# Revit family: NWL_Elevator_Artisan_Rectangular_42x32
name_source: partatom
category: Specialty Equipment
units: mm (PartAtom-declared; Revit-internal decimal feet)

## family parameters
Always vertical = Yes
Cut with Voids When Loaded = No
Enable Cutting in Views = No
Maintain Annotation Orientation = No
Part Type = Normal
Room Calculation Point = No
Round Connector Dimension = Use Diameter
Shared = No
Work Plane-Based = No

## types (1)
- NWL_Elevator_Artisan_Rectangular_42x32
    Cab_Height = 78 "
    Construction Details = https://www.arcat.com
    Default Elevation = 0 "
    Frame = Steel
    Glass = Glass
    Green Building-LEED = https://www.arcat.com
    Hoistway_Length = 39.106 "
    Hoistway_Width = 28.106 "
    Load = 30 VA
    Machine_Height = 18 "
    Manufacturer = Nationwide Lifts
    Manufacturer Fax = (877) 825-6001
    Manufacturer Website = https://www.elevators.com
    Model = Artisan Rectangular 42x32
    Platform_Length = 36.606 "
    Platform_Width = 25.606 "
    Poles = 1
    Product Data = https://www.arcat.com
    Ring_Length = 42 "
    Ring_Width = 32 "
    Specification = https://www.arcat.com
    URL = https://www.elevators.com
    Voltage = 230 V

## geometry (parser evidence)
native form markers: Sweep x5
no freeform markers — native parametric forms only
